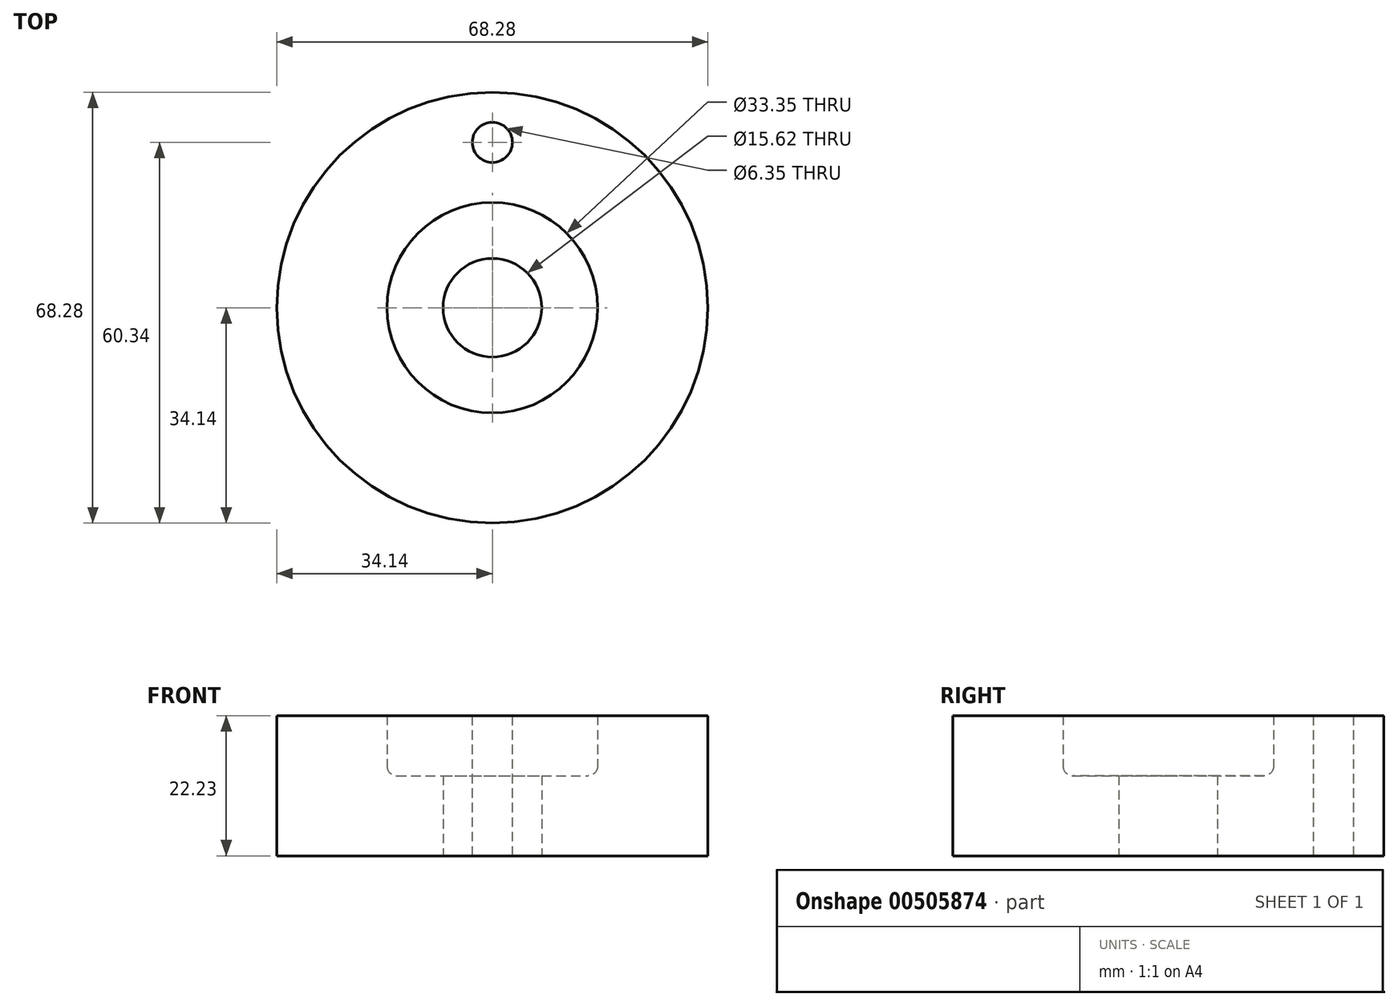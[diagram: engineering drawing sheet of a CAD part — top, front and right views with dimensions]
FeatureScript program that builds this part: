
annotation { "Feature Type Name" : "Feature", "Feature Type Description" : "" }
export const myFeature = defineFeature(function(context is Context, id is Id, definition is map)
    precondition{}
    {
        {
            var Q0;
            Q0=qCreatedBy(makeId("Front.planeOp"),FACE);
            var sketch = newSketch(context, id + "F0", { "sketchPlane" : qUnion([Q0])});
            skLineSegment(sketch, "E0", {"start": v(34.14, 0) * mm, "end": v(34.14, 22.23) * mm});
            skLineSegment(sketch, "E1", {"start": v(34.14, 22.23) * mm, "end": v(16.68, 22.23) * mm});
            skLineSegment(sketch, "E2", {"start": v(0, 0) * mm, "end": v(0, 12.7) * mm, "construction": true});
            skLineSegment(sketch, "E3", {"start": v(16.68, 22.23) * mm, "end": v(16.68, 14.22) * mm});
            skArc(sketch, "E4", {"start": v(15.15, 12.7) * mm, "mid": v(16.23, 13.15) * mm, "end": v(16.68, 14.22) * mm});
            skLineSegment(sketch, "E5", {"start": v(15.15, 12.7) * mm, "end": v(7.81, 12.7) * mm});
            skLineSegment(sketch, "E6", {"start": v(7.81, 12.7) * mm, "end": v(0, 12.7) * mm, "construction": true});
            skLineSegment(sketch, "E7", {"start": v(34.14, 0) * mm, "end": v(7.81, 0) * mm});
            skLineSegment(sketch, "E8", {"start": v(7.81, 0) * mm, "end": v(7.81, 12.7) * mm});
            skLineSegment(sketch, "E9", {"start": v(7.81, 0) * mm, "end": v(0, 0) * mm, "construction": true});
            skSolve(sketch);
        }
        {
            var Q0;
            Q0=makeQuery(id+"F0.imprint","IMPRINT",FACE,{"disambiguationData":[TD([[makeQuery(id+"F0.imprint","IMPRINT",EDGE,{"derivedFrom":sQuery(id+"F0.wireOp",EDGE,"E0")}),1.0]])]});
            var Q1;
            Q1=sQuery(id+"F0.wireOp",EDGE,"E2");
            revolve(context, id + "F1", {"entities" : qUnion([Q0]), "axis" : qUnion([Q1]), "revolveType" : RevolveType.FULL});
        }
        {
            var Q0;
            Q0=makeQuery(id+"F1.opRevolve","SWEPT_FACE",FACE,{"disambiguationData":[OSD([sQuery(id+"F0.wireOp",EDGE,"E1")])]});
            var sketch = newSketch(context, id + "F2", { "sketchPlane" : qUnion([Q0])});
            skCircle(sketch, "E10", {"center": v(0, 0) * mm, "radius": 26.2 * mm, "construction": true});
            skCircle(sketch, "E11", {"center": v(0, 26.2) * mm, "radius": 3.18 * mm});
            skSolve(sketch);
        }
        {
            var Q0;
            Q0=makeQuery(id+"F2.imprint","IMPRINT",FACE,{"disambiguationData":[TD([[makeQuery(id+"F2.imprint","IMPRINT",EDGE,{"derivedFrom":sQuery(id+"F2.wireOp",EDGE,"E11")}),1.0]])]});
            extrude(context, id + "F3", {"entities" : qUnion([Q0]), "operationType" : NewBodyOperationType.REMOVE, "endBound" : BoundingType.THROUGH_ALL, "oppositeDirection" : true, "depth" : 25.4 * mm});
        }
    });
